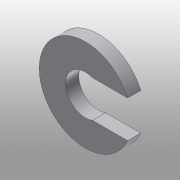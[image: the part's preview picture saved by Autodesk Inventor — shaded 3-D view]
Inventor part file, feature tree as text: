
AUTODESK INVENTOR PART (.ipt)
format: ipt  version: 2016 (Build 200138000, 138)  size: 97,280 bytes
history: native  units: mm
features: extrude x2, sketch x2
ambient origin geometry x8: Origin, YZ Plane, XZ Plane, XY Plane, X Axis, Y Axis, Z Axis, Center Point
bodies: Solid1 (feature_tree)
feature tree (4):
  extrude  "Extrusion1"  Depth=2.8mm
  extrude  "Extrusion2"  Depth=3.0mm TaperAngle=0.0deg
  sketch  "Sketch1"  dims[d0=7.0mm d1=2.8mm]
  sketch  "Sketch2"  dims[d2=1.5mm d3=3.0mm d4=0.0mm d5=2.0mm d6=0.0mm]
